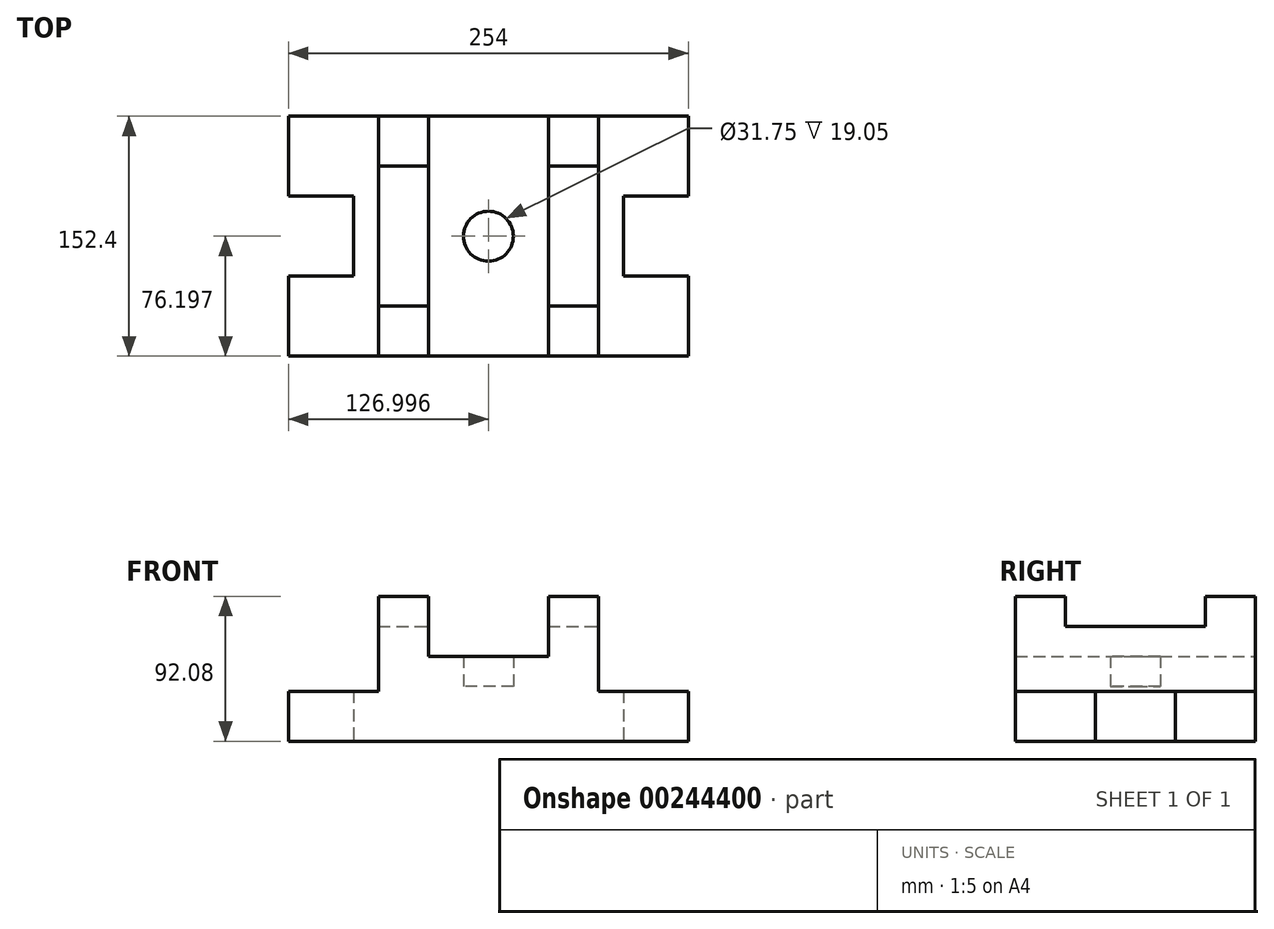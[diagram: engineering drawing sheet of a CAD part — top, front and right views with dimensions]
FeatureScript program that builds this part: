
annotation { "Feature Type Name" : "Feature", "Feature Type Description" : "" }
export const myFeature = defineFeature(function(context is Context, id is Id, definition is map)
    precondition{}
    {
        {
            var Q0;
            Q0=qCreatedBy(makeId("Top.planeOp"),FACE);
            var sketch = newSketch(context, id + "F0", { "sketchPlane" : qUnion([Q0])});
            skLineSegment(sketch, "E0", {"start": v(-118.54, -79.35) * mm, "end": v(135.46, -79.35) * mm});
            skLineSegment(sketch, "E1", {"start": v(135.46, -79.35) * mm, "end": v(135.46, -28.55) * mm});
            skLineSegment(sketch, "E2", {"start": v(-118.54, -79.35) * mm, "end": v(-118.54, -28.55) * mm});
            skLineSegment(sketch, "E3", {"start": v(-118.54, -28.55) * mm, "end": v(-77.27, -28.55) * mm});
            skLineSegment(sketch, "E4", {"start": v(135.46, -28.55) * mm, "end": v(94.18, -28.55) * mm});
            skLineSegment(sketch, "E5", {"start": v(-77.27, -28.55) * mm, "end": v(-77.27, 22.25) * mm});
            skLineSegment(sketch, "E6", {"start": v(94.18, -28.55) * mm, "end": v(94.18, 22.25) * mm});
            skLineSegment(sketch, "E7", {"start": v(-77.27, 22.25) * mm, "end": v(-118.54, 22.25) * mm});
            skLineSegment(sketch, "E8", {"start": v(94.18, 22.25) * mm, "end": v(135.46, 22.25) * mm});
            skLineSegment(sketch, "E9", {"start": v(-118.54, 22.25) * mm, "end": v(-118.54, 73.05) * mm});
            skLineSegment(sketch, "E10", {"start": v(-118.54, 73.05) * mm, "end": v(135.46, 73.05) * mm});
            skLineSegment(sketch, "E11", {"start": v(135.46, 73.05) * mm, "end": v(135.46, 22.25) * mm});
            skLineSegment(sketch, "E12", {"start": v(-61.4, 41.3) * mm, "end": v(-29.64, 41.3) * mm});
            skLineSegment(sketch, "E13", {"start": v(-61.4, -47.6) * mm, "end": v(-29.64, -47.6) * mm});
            skLineSegment(sketch, "E14", {"start": v(46.56, 41.3) * mm, "end": v(78.3, 41.3) * mm});
            skLineSegment(sketch, "E15", {"start": v(46.56, -47.6) * mm, "end": v(78.3, -47.6) * mm});
            skCircle(sketch, "E16", {"center": v(8.46, -3.15) * mm, "radius": 15.88 * mm});
            skLineSegment(sketch, "E17", {"start": v(-61.4, 41.3) * mm, "end": v(-61.4, 73.05) * mm});
            skLineSegment(sketch, "E18", {"start": v(-61.4, 41.3) * mm, "end": v(-61.4, -47.6) * mm});
            skLineSegment(sketch, "E19", {"start": v(-61.4, -47.6) * mm, "end": v(-61.4, -79.35) * mm});
            skLineSegment(sketch, "E20", {"start": v(-29.64, 41.3) * mm, "end": v(-29.64, 73.05) * mm});
            skLineSegment(sketch, "E21", {"start": v(-29.64, 41.3) * mm, "end": v(-29.64, -47.6) * mm});
            skLineSegment(sketch, "E22", {"start": v(-29.64, -47.6) * mm, "end": v(-29.64, -79.35) * mm});
            skLineSegment(sketch, "E23", {"start": v(46.56, -79.35) * mm, "end": v(46.56, -47.6) * mm});
            skLineSegment(sketch, "E24", {"start": v(46.56, -47.6) * mm, "end": v(46.56, 41.3) * mm});
            skLineSegment(sketch, "E25", {"start": v(46.56, 73.05) * mm, "end": v(46.56, 41.3) * mm});
            skLineSegment(sketch, "E26", {"start": v(78.3, -47.6) * mm, "end": v(78.3, -79.35) * mm});
            skLineSegment(sketch, "E27", {"start": v(78.3, -47.6) * mm, "end": v(78.3, 41.3) * mm});
            skLineSegment(sketch, "E28", {"start": v(78.3, 73.05) * mm, "end": v(78.3, 41.3) * mm});
            skSolve(sketch);
        }
        {
            var Q0;
            {var subQ5=sQuery(id+"F0.wireOp",EDGE,"E12");Q0=makeQuery(id+"F0.imprint","IMPRINT",FACE,{"disambiguationData":[TD([[makeQuery(id+"F0.imprint","IMPRINT",EDGE,{"derivedFrom":subQ5}),1.0]])]});}
            var Q1;
            {var subQ5=sQuery(id+"F0.wireOp",EDGE,"E13");Q1=makeQuery(id+"F0.imprint","IMPRINT",FACE,{"disambiguationData":[TD([[makeQuery(id+"F0.imprint","IMPRINT",EDGE,{"derivedFrom":subQ5}),-1.0]])]});}
            var Q2;
            {var subQ5=sQuery(id+"F0.wireOp",EDGE,"E14");Q2=makeQuery(id+"F0.imprint","IMPRINT",FACE,{"disambiguationData":[TD([[makeQuery(id+"F0.imprint","IMPRINT",EDGE,{"derivedFrom":subQ5}),1.0]])]});}
            var Q3;
            {var subQ5=sQuery(id+"F0.wireOp",EDGE,"E15");Q3=makeQuery(id+"F0.imprint","IMPRINT",FACE,{"disambiguationData":[TD([[makeQuery(id+"F0.imprint","IMPRINT",EDGE,{"derivedFrom":subQ5}),-1.0]])]});}
            extrude(context, id + "F1", {"entities" : qUnion([Q0, Q1, Q2, Q3]), "depth" : 92.07 * mm});
        }
        {
            var Q0;
            Q0=makeQuery(id+"F0.imprint","IMPRINT",FACE,{"disambiguationData":[TD([[makeQuery(id+"F0.imprint","IMPRINT",EDGE,{"derivedFrom":sQuery(id+"F0.wireOp",EDGE,"E16")}),-1.0]])]});
            extrude(context, id + "F2", {"entities" : qUnion([Q0]), "operationType" : NewBodyOperationType.ADD, "depth" : 53.97 * mm});
        }
        {
            var Q0;
            Q0=makeQuery(id+"F0.imprint","IMPRINT",FACE,{"disambiguationData":[TD([[makeQuery(id+"F0.imprint","IMPRINT",EDGE,{"derivedFrom":sQuery(id+"F0.wireOp",EDGE,"E16")}),1.0]])]});
            extrude(context, id + "F3", {"entities" : qUnion([Q0]), "operationType" : NewBodyOperationType.ADD, "depth" : 34.92 * mm});
        }
        {
            var Q0;
            {var subQ0=sQuery(id+"F0.wireOp",EDGE,"E12");Q0=makeQuery(id+"F0.imprint","IMPRINT",FACE,{"disambiguationData":[TD([[makeQuery(id+"F0.imprint","IMPRINT",EDGE,{"derivedFrom":subQ0}),-1.0]])]});}
            var Q1;
            {var subQ0=sQuery(id+"F0.wireOp",EDGE,"E14");Q1=makeQuery(id+"F0.imprint","IMPRINT",FACE,{"disambiguationData":[TD([[makeQuery(id+"F0.imprint","IMPRINT",EDGE,{"derivedFrom":subQ0}),-1.0]])]});}
            extrude(context, id + "F4", {"entities" : qUnion([Q0, Q1]), "depth" : 73.02 * mm});
        }
        {
            var Q0;
            {var subQ7=sQuery(id+"F0.wireOp",EDGE,"E2");Q0=makeQuery(id+"F0.imprint","IMPRINT",FACE,{"disambiguationData":[TD([[makeQuery(id+"F0.imprint","IMPRINT",EDGE,{"derivedFrom":subQ7}),-1.0]])]});}
            var Q1;
            {var subQ0=sQuery(id+"F0.wireOp",EDGE,"E1");Q1=makeQuery(id+"F0.imprint","IMPRINT",FACE,{"disambiguationData":[TD([[makeQuery(id+"F0.imprint","IMPRINT",EDGE,{"derivedFrom":subQ0}),1.0]])]});}
            extrude(context, id + "F5", {"entities" : qUnion([Q0, Q1]), "operationType" : NewBodyOperationType.ADD, "depth" : 31.75 * mm});
        }
    });
